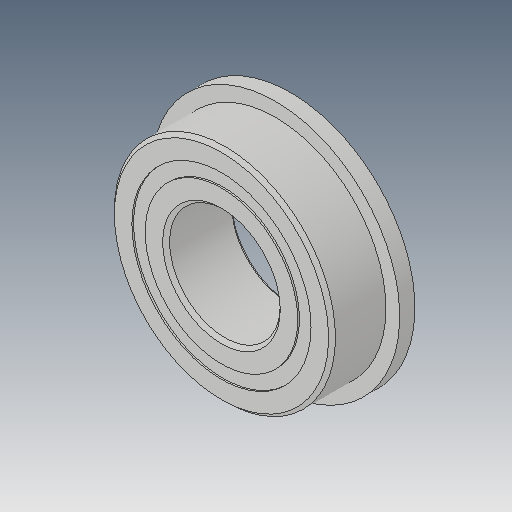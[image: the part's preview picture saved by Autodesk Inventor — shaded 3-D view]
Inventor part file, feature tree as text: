
AUTODESK INVENTOR PART (.ipt)
format: ipt  version: 2018 (Build 220112000, 112)  size: 602,112 bytes
history: native  units: in
note: dims shown in document units (in); Inventor stores cm internally (conversion verified against a paired STEP export)
features: other x11, revolve x5
ambient origin geometry x8: Origin, YZ Plane, XZ Plane, XY Plane, X Axis, Y Axis, Z Axis, Center Point
bodies: Solid1 (feature_tree), Solid2 (feature_tree), Solid3 (feature_tree), Solid4 (feature_tree), Solid5 (feature_tree), Solid6 (feature_tree), Solid7 (feature_tree), Solid8 (feature_tree), Solid9 (feature_tree), Solid10 (feature_tree), Solid11 (feature_tree), Solid12 (feature_tree), Solid13 (feature_tree), Solid14 (feature_tree), Solid15 (feature_tree), Solid16 (feature_tree)
feature tree (16):
  revolve  "Revolve3"  [1 undecoded]
  revolve  "Revolve4"  [1 undecoded]
  other  "CirPattern1[1]"
  other  "CirPattern1[2]"
  other  "CirPattern1[3]"
  other  "CirPattern1[4]"
  other  "CirPattern1[5]"
  other  "CirPattern1[6]"
  other  "CirPattern1[7]"
  other  "CirPattern1[8]"
  other  "CirPattern1[9]"
  other  "CirPattern1[10]"
  other  "CirPattern1[11]"
  revolve  "Revolve5[1]"  [1 undecoded]
  revolve  "Revolve5[2]"  [1 undecoded]
  revolve  "Revolve6"  [1 undecoded]
note: 5 required parameter values undecoded (feature->parameter linkage not recoverable at this tier; creation-order binding heuristic only, values carry confidence <= 0.55)
